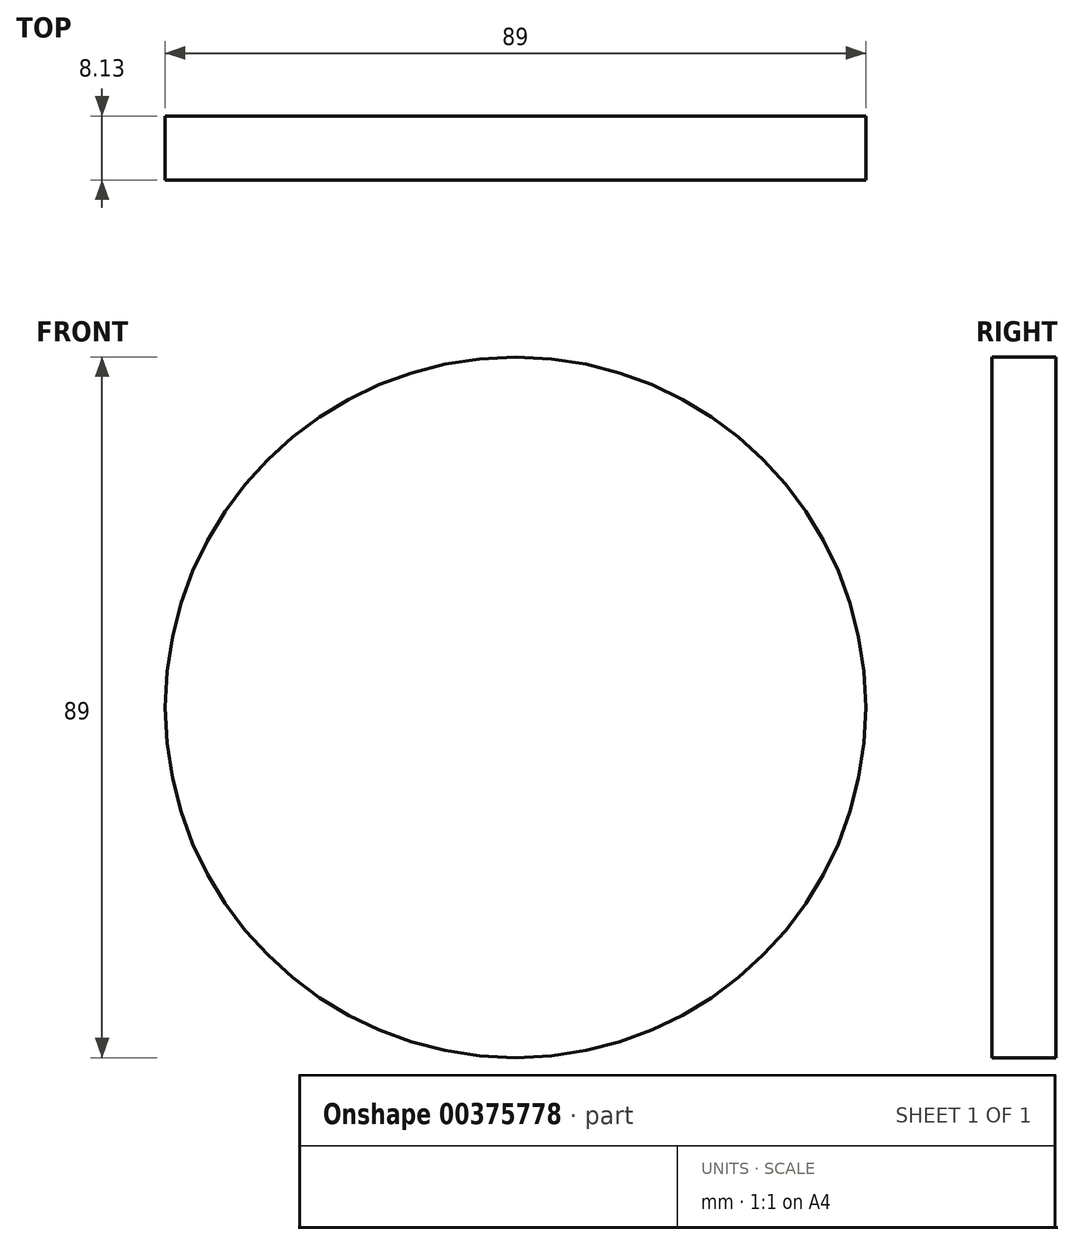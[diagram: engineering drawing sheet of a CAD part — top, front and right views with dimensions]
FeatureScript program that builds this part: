
annotation { "Feature Type Name" : "Feature", "Feature Type Description" : "" }
export const myFeature = defineFeature(function(context is Context, id is Id, definition is map)
    precondition{}
    {
        {
            var Q0;
            Q0=qCreatedBy(makeId("Front.planeOp"),FACE);
            var sketch = newSketch(context, id + "F0", { "sketchPlane" : qUnion([Q0])});
            skCircle(sketch, "E0", {"center": v(0, 0) * mm, "radius": 44.5 * mm});
            skSolve(sketch);
        }
        {
            var Q0;
            Q0 = qSketchRegion(id + "F0", true);
            extrude(context, id + "F1", {"entities" : qUnion([Q0]), "depth" : 8.13 * mm});
        }
    });
